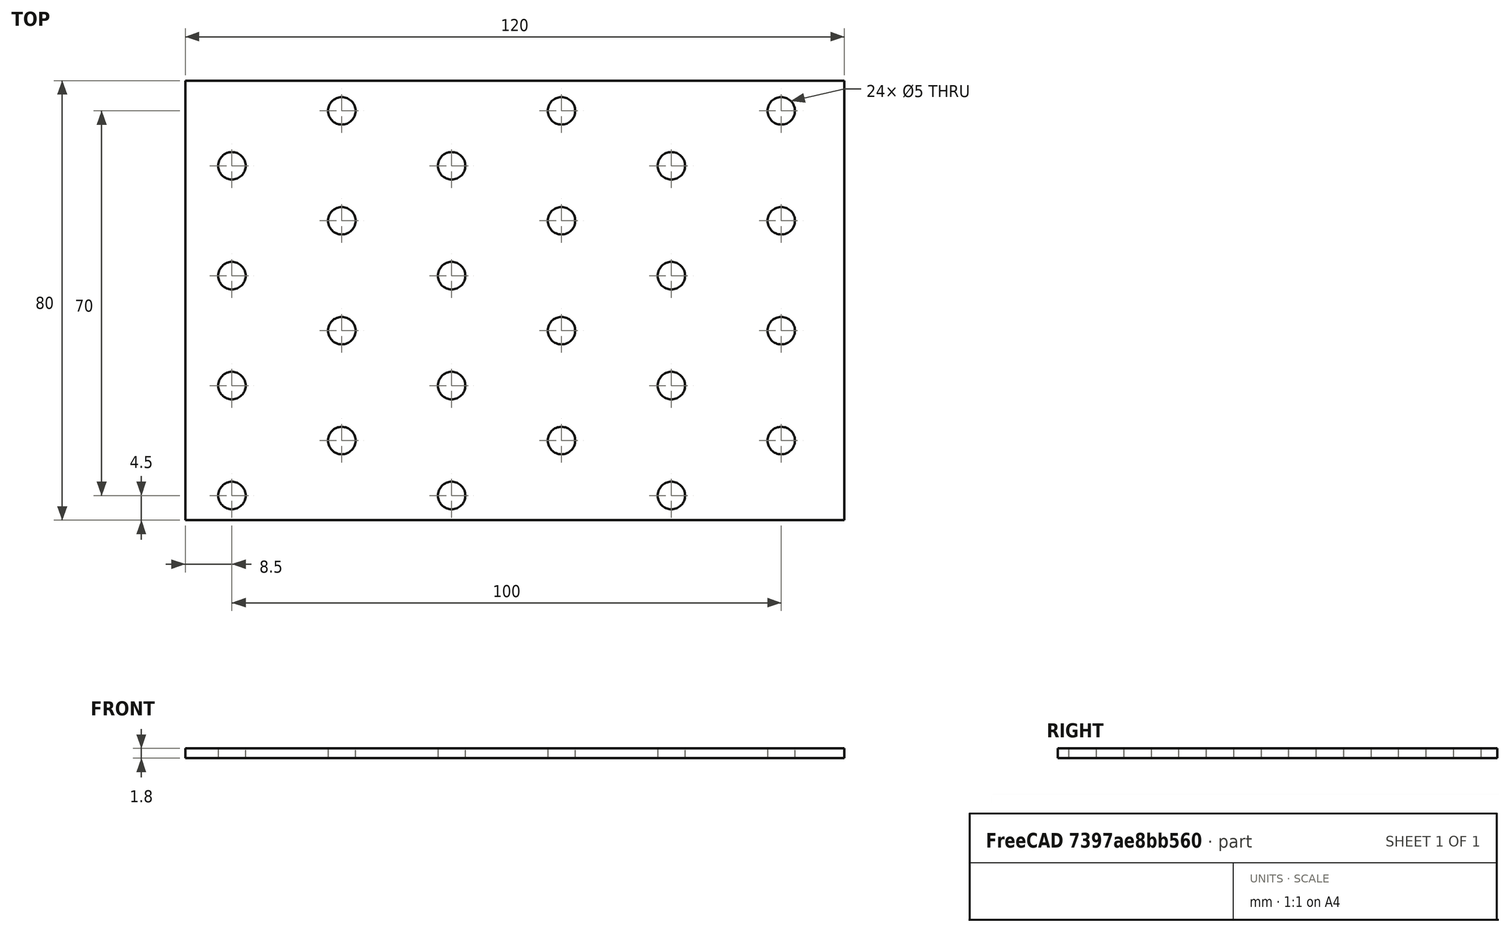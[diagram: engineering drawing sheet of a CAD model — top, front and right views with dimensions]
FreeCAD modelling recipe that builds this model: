
FCSTD DOCUMENT  (FreeCAD 0.19R24276 (Git))
Label: 80x120__1_8mm_p1
License: All rights reserved
LicenseURL: http://en.wikipedia.org/wiki/All_rights_reserved
objects: Sketcher::SketchObject×2, PartDesign::Pad×1, PartDesign::Body×1
note: 5 computed .brp shape members not serialized (recipe doc carries the construction recipe); baked Part::Feature solids carry a one-line shape summary decoded from their .brp

FEATURE [Sketcher::SketchObject] Sketch
  FullyConstrained = false
  MapMode = 5
  Support = -> [XY_Plane]
  sketch-geometry (46):
    g0: LineSegment StartX=0 StartY=0 StartZ=0 EndX=120 EndY=0 EndZ=0
    g1: LineSegment StartX=120 StartY=0 StartZ=0 EndX=120 EndY=80 EndZ=0
    g2: LineSegment StartX=120 StartY=80 StartZ=0 EndX=0 EndY=80 EndZ=0
    g3: LineSegment StartX=0 StartY=80 StartZ=0 EndX=0 EndY=0 EndZ=0
    g4: LineSegment StartX=0 StartY=4.5 StartZ=0 EndX=120 EndY=4.5 EndZ=0
    g5: LineSegment StartX=0 StartY=24.5 StartZ=0 EndX=120 EndY=24.5 EndZ=0
    g6: LineSegment StartX=0 StartY=44.5 StartZ=0 EndX=120 EndY=44.5 EndZ=0
    g7: LineSegment StartX=0 StartY=64.5 StartZ=0 EndX=120 EndY=64.5 EndZ=0
    g8: LineSegment StartX=48.5 StartY=0 StartZ=0 EndX=48.5 EndY=4.5 EndZ=0
    g9: LineSegment StartX=68.5 StartY=0 StartZ=0 EndX=68.5 EndY=4.5 EndZ=0
    g10: LineSegment StartX=88.5 StartY=0 StartZ=0 EndX=88.5 EndY=4.5 EndZ=0
    g11: LineSegment StartX=108.5 StartY=0 StartZ=0 EndX=108.5 EndY=4.5 EndZ=0
    g12: LineSegment StartX=0 StartY=14.5 StartZ=0 EndX=120 EndY=14.5 EndZ=0
    g13: LineSegment StartX=0 StartY=34.5 StartZ=0 EndX=120 EndY=34.5 EndZ=0
    g14: LineSegment StartX=0 StartY=54.5 StartZ=0 EndX=120 EndY=54.5 EndZ=0
    g15: LineSegment StartX=0 StartY=74.5 StartZ=0 EndX=120 EndY=74.5 EndZ=0
    g16: LineSegment StartX=48.5 StartY=24.5 StartZ=0 EndX=48.5 EndY=80 EndZ=0
    g17: LineSegment StartX=68.5 StartY=14.5 StartZ=0 EndX=68.5 EndY=80 EndZ=0
    g18: LineSegment StartX=88.5 StartY=24.5 StartZ=0 EndX=88.5 EndY=80 EndZ=0
    g19: LineSegment StartX=108.5 StartY=14.5 StartZ=0 EndX=108.5 EndY=80 EndZ=0
    g20: Circle CenterX=8.5 CenterY=4.5 CenterZ=0 NormalX=0 NormalY=0 NormalZ=1 AngleXU=0 Radius=2.5
    g21: Circle CenterX=48.5 CenterY=4.5 CenterZ=0 NormalX=0 NormalY=0 NormalZ=1 AngleXU=0 Radius=2.5
    g22: Circle CenterX=88.5 CenterY=4.5 CenterZ=0 NormalX=0 NormalY=0 NormalZ=1 AngleXU=0 Radius=2.5
    g23: Circle CenterX=28.5 CenterY=14.5 CenterZ=0 NormalX=0 NormalY=0 NormalZ=1 AngleXU=0 Radius=2.5
    g24: Circle CenterX=108.5 CenterY=14.5 CenterZ=0 NormalX=0 NormalY=0 NormalZ=1 AngleXU=0 Radius=2.5
    g25: Circle CenterX=8.5 CenterY=24.5 CenterZ=0 NormalX=0 NormalY=0 NormalZ=1 AngleXU=0 Radius=2.5
    g26: Circle CenterX=48.5 CenterY=24.5 CenterZ=0 NormalX=0 NormalY=0 NormalZ=1 AngleXU=0 Radius=2.5
    g27: Circle CenterX=88.5 CenterY=24.5 CenterZ=0 NormalX=0 NormalY=0 NormalZ=1 AngleXU=0 Radius=2.5
    g28: Circle CenterX=8.5 CenterY=44.5 CenterZ=0 NormalX=0 NormalY=0 NormalZ=1 AngleXU=0 Radius=2.5
    g29: Circle CenterX=48.5 CenterY=44.5 CenterZ=0 NormalX=0 NormalY=0 NormalZ=1 AngleXU=0 Radius=2.5
    g30: Circle CenterX=88.5 CenterY=44.5 CenterZ=0 NormalX=0 NormalY=0 NormalZ=1 AngleXU=0 Radius=2.5
    g31: Circle CenterX=28.5 CenterY=54.5 CenterZ=0 NormalX=0 NormalY=0 NormalZ=1 AngleXU=0 Radius=2.5
    g32: Circle CenterX=68.5 CenterY=54.5 CenterZ=0 NormalX=0 NormalY=0 NormalZ=1 AngleXU=0 Radius=2.5
    g33: Circle CenterX=108.5 CenterY=54.5 CenterZ=0 NormalX=0 NormalY=0 NormalZ=1 AngleXU=0 Radius=2.5
    g34: Circle CenterX=88.5 CenterY=64.5 CenterZ=0 NormalX=0 NormalY=0 NormalZ=1 AngleXU=0 Radius=2.5
    g35: Circle CenterX=48.5 CenterY=64.5 CenterZ=0 NormalX=0 NormalY=0 NormalZ=1 AngleXU=0 Radius=2.5
    g36: Circle CenterX=8.5 CenterY=64.5 CenterZ=0 NormalX=0 NormalY=0 NormalZ=1 AngleXU=0 Radius=2.5
    g37: Circle CenterX=28.5 CenterY=34.5 CenterZ=0 NormalX=0 NormalY=0 NormalZ=1 AngleXU=0 Radius=2.5
    g38: Circle CenterX=68.5 CenterY=34.5 CenterZ=0 NormalX=0 NormalY=0 NormalZ=1 AngleXU=0 Radius=2.5
    g39: Circle CenterX=108.5 CenterY=34.5 CenterZ=0 NormalX=0 NormalY=0 NormalZ=1 AngleXU=0 Radius=2.5
    g40: Circle CenterX=28.5 CenterY=74.5 CenterZ=0 NormalX=0 NormalY=0 NormalZ=1 AngleXU=0 Radius=2.5
    g41: Circle CenterX=68.5 CenterY=74.5 CenterZ=0 NormalX=0 NormalY=0 NormalZ=1 AngleXU=0 Radius=2.5
    g42: Circle CenterX=108.5 CenterY=74.5 CenterZ=0 NormalX=0 NormalY=0 NormalZ=1 AngleXU=0 Radius=2.5
    g43: LineSegment StartX=28.5 StartY=74.5 StartZ=0 EndX=28.5 EndY=14.5 EndZ=0
    g44: LineSegment StartX=8.5 StartY=4.5 StartZ=0 EndX=8.5 EndY=24.5 EndZ=0
    g45: Circle CenterX=68.5 CenterY=14.5 CenterZ=0 NormalX=0 NormalY=0 NormalZ=1 AngleXU=0 Radius=2.5
  constraints (100):
    c: Coincident(g0,g1)
    c: Coincident(g1,g2)
    c: Coincident(g2,g3)
    c: Coincident(g3,g0)
    c: Horizontal(g0)
    c: Horizontal(g2)
    c: Vertical(g1)
    c: Vertical(g3)
    c: Coincident(g0,g-1)
    c: DistanceX(g0,g0) = 120
    c: DistanceY(g3,g3) = 80
    c: Horizontal(g4)
    c: PointOnObject(g4,g3)
    c: PointOnObject(g4,g1)
    c: Horizontal(g5)
    c: PointOnObject(g5,g3)
    c: PointOnObject(g5,g1)
    c: DistanceY(g4,g5) = 20
    c: Horizontal(g6)
    c: PointOnObject(g6,g1)
    c: PointOnObject(g6,g3)
    c: DistanceY(g5,g6) = 20
    c: Horizontal(g7)
    c: PointOnObject(g7,g1)
    c: PointOnObject(g7,g3)
    c: DistanceY(g6,g7) = 20
    c: Vertical(g8)
    c: Vertical(g9)
    c: Vertical(g10)
    c: Vertical(g11)
    c: PointOnObject(g8,g0)
    c: PointOnObject(g9,g0)
    c: PointOnObject(g10,g0)
    c: PointOnObject(g11,g0)
    c: PointOnObject(g19,g2)
    c: PointOnObject(g18,g2)
    c: PointOnObject(g17,g2)
    c: PointOnObject(g16,g2)
    c: DistanceX(g8,g9) = 20
    c: DistanceX(g9,g10) = 20
    c: DistanceX(g10,g11) = 20
    c: Horizontal(g12)
    c: Horizontal(g13)
    c: Horizontal(g14)
    c: Horizontal(g15)
    c: PointOnObject(g12,g3)
    c: PointOnObject(g13,g3)
    c: PointOnObject(g14,g3)
    c: PointOnObject(g15,g3)
    c: PointOnObject(g15,g1)
    c: PointOnObject(g14,g1)
    c: PointOnObject(g13,g1)
    c: PointOnObject(g12,g1)
    c: DistanceY(g0,g12) = 14.5
    c: DistanceY(g12,g13) = 20
    c: DistanceY(g13,g14) = 20
    c: DistanceY(g14,g15) = 20
    c: PointOnObject(g20,g4)
    c: PointOnObject(g23,g12)
    c: PointOnObject(g8,g4)
    c: Tangent(g8,g16)
    c: PointOnObject(g9,g4)
    c: PointOnObject(g17,g12)
    c: Tangent(g9,g17)
    c: PointOnObject(g10,g4)
    c: Tangent(g10,g18)
    c: PointOnObject(g11,g4)
    c: PointOnObject(g19,g12)
    c: Tangent(g11,g19)
    c: Coincident(g21,g8)
    c: Coincident(g22,g10)
    c: Coincident(g24,g19)
    c: Equal(g20,g23)
    c: Equal(g23,g21)
    c: Equal(g21,g22)
    c: Equal(g22,g24)
    c: Diameter(g23) = 5
    c: PointOnObject(g16,g5)
    c: PointOnObject(g18,g5)
    c: Equal(g26,g27)
    c: Equal(g36,g31)
    c: Equal(g31,g35)
    c: Equal(g35,g34)
    c: Equal(g34,g33)
    c: Diameter(g31) = 5
    c: Equal(g34,g32)
    c: Equal(g29,g30)
    c: Diameter(g37) = 5
    c: Diameter(g40) = 5
    c: Coincident(g43,g40)
    c: Coincident(g43,g23)
    c: Vertical(g43)
    c: DistanceX(g20,g23) = 20
    c: DistanceX(g0,g20) = 8.5
    c: DistanceY(g0,g4) = 4.5
    c: Coincident(g44,g20)
    c: Coincident(g44,g25)
    c: Vertical(g44)
    c: Coincident(g45,g17)
    c: Equal(g24,g45)
FEATURE [PartDesign::Pad] Pad
  Direction = (1,1,1)
  Length = 1.8
  Length2 = 100
  Profile = -> Sketch
  Type = 0
FEATURE [Sketcher::SketchObject] Sketch001
  FullyConstrained = false
  MapMode = 5
  Placement = pos=(0,0,1.8) rot=(0,0,1;0rad)
  Support = -> [Pad]
  sketch-geometry (18):
    g0: LineSegment StartX=20.3352 StartY=44.946 StartZ=0 EndX=69.3352 EndY=44.946 EndZ=0
    g1: LineSegment StartX=69.3352 StartY=44.946 StartZ=0 EndX=69.3352 EndY=94.946 EndZ=0
    g2: LineSegment StartX=69.3352 StartY=94.946 StartZ=0 EndX=20.3352 EndY=94.946 EndZ=0
    g3: LineSegment StartX=15.3352 StartY=89.946 StartZ=0 EndX=15.3352 EndY=49.946 EndZ=0
    g4: LineSegment StartX=15.3352 StartY=49.946 StartZ=0 EndX=20.3352 EndY=44.946 EndZ=0
    g5: LineSegment StartX=15.3352 StartY=89.946 StartZ=0 EndX=20.3352 EndY=94.946 EndZ=0
    g6: LineSegment StartX=194.898 StartY=-97.9756 StartZ=0 EndX=243.898 EndY=-97.9756 EndZ=0
    g7: LineSegment StartX=243.898 StartY=-97.9756 StartZ=0 EndX=243.898 EndY=-47.9756 EndZ=0
    g8: LineSegment StartX=243.898 StartY=-47.9756 StartZ=0 EndX=194.898 EndY=-47.9756 EndZ=0
    g9: LineSegment StartX=189.898 StartY=-52.9756 StartZ=0 EndX=189.898 EndY=-92.9756 EndZ=0
    g10: LineSegment StartX=189.898 StartY=-92.9756 StartZ=0 EndX=194.898 EndY=-97.9756 EndZ=0
    g11: LineSegment StartX=189.898 StartY=-52.9756 StartZ=0 EndX=194.898 EndY=-47.9756 EndZ=0
    g12: LineSegment StartX=39.8661 StartY=-6.14346 StartZ=0 EndX=88.8661 EndY=-6.14346 EndZ=0
    g13: LineSegment StartX=88.8661 StartY=-6.14346 StartZ=0 EndX=88.8661 EndY=43.8565 EndZ=0
    g14: LineSegment StartX=88.8661 StartY=43.8565 StartZ=0 EndX=39.8661 EndY=43.8565 EndZ=0
    g15: LineSegment StartX=34.8661 StartY=38.8565 StartZ=0 EndX=34.8661 EndY=-1.14346 EndZ=0
    g16: LineSegment StartX=34.8661 StartY=-1.14346 StartZ=0 EndX=39.8661 EndY=-6.14346 EndZ=0
    g17: LineSegment StartX=34.8661 StartY=38.8565 StartZ=0 EndX=39.8661 EndY=43.8565 EndZ=0
  constraints (48):
    c: Coincident(g0,g1)
    c: Coincident(g1,g2)
    c: Horizontal(g0)
    c: Horizontal(g2)
    c: Vertical(g1)
    c: Vertical(g3)
    c: DistanceY(g1,g1) = 50
    c: Coincident(g0,g4)
    c: Coincident(g3,g4)
    c: Coincident(g3,g5)
    c: Coincident(g2,g5)
    c: DistanceY(g5,g5) = 5
    c: DistanceX(g3,g0) = 54
    c: DistanceX(g5,g5) = 5
    c: DistanceX(g3,g0) = 5
    c: DistanceY(g0,g3) = 5
    c: Coincident(g6,g7)
    c: Coincident(g7,g8)
    c: Horizontal(g6)
    c: Horizontal(g8)
    c: Vertical(g7)
    c: Vertical(g9)
    c: Equal(g1,g7) = 50
    c: Coincident(g6,g10)
    c: Coincident(g9,g10)
    c: Coincident(g9,g11)
    c: Coincident(g8,g11)
    c: Equal(g5,g11) = 5
    c: DistanceX(g9,g6) = 54
    c: DistanceX(g9,g6) = 5
    c: DistanceY(g6,g9) = 5
    c: DistanceX(g9,g8) = 5
    c: Coincident(g12,g13)
    c: Coincident(g13,g14)
    c: Horizontal(g12)
    c: Horizontal(g14)
    c: Vertical(g13)
    c: Vertical(g15)
    c: Coincident(g12,g16)
    c: Coincident(g15,g16)
    c: Coincident(g15,g17)
    c: Coincident(g14,g17)
    c: DistanceX(g15,g12) = 54
    c: DistanceX(g15,g12) = 5
    c: DistanceY(g12,g15) = 5
    c: DistanceX(g15,g14) = 5
    c: DistanceY(g13,g13) = 50
    c: DistanceY(g15,g14) = 5
FEATURE [PartDesign::Body] Body
  Group = -> [Sketch,Pad,Sketch001]
  Origin = -> Origin
  Tip = -> Pad
